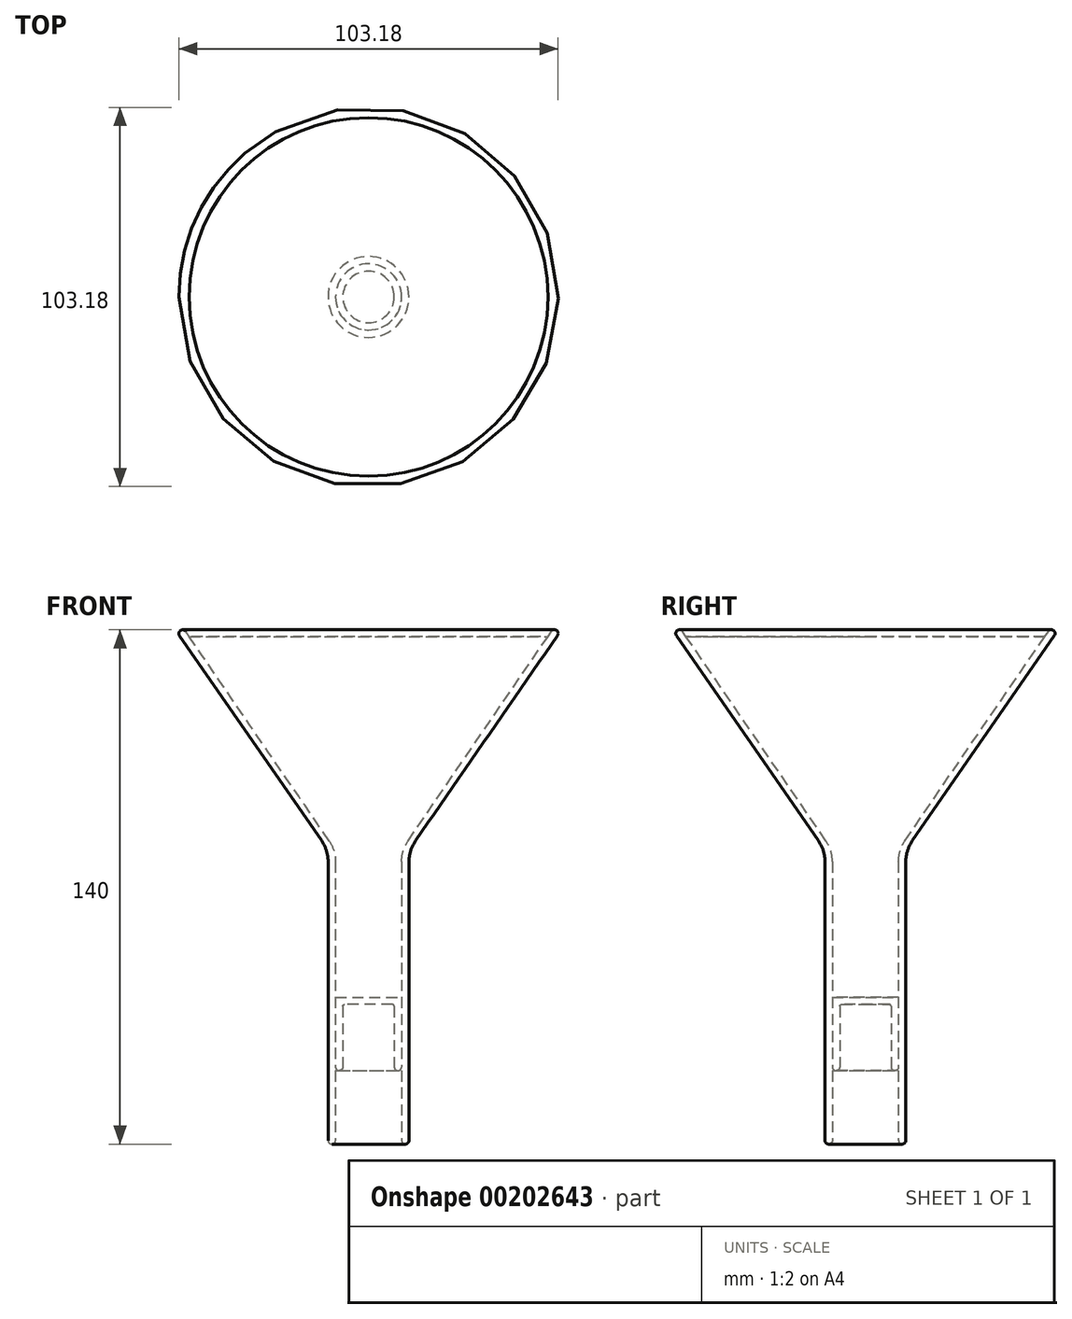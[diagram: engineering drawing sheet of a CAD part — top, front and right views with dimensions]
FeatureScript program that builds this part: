
annotation { "Feature Type Name" : "Feature", "Feature Type Description" : "" }
export const myFeature = defineFeature(function(context is Context, id is Id, definition is map)
    precondition{}
    {
        {
            var Q0;
            Q0=qCreatedBy(makeId("Front.planeOp"),FACE);
            var sketch = newSketch(context, id + "F0", { "sketchPlane" : qUnion([Q0])});
            skLineSegment(sketch, "E0", {"start": v(0, 91.4) * mm, "end": v(0, -48.6) * mm});
            skLineSegment(sketch, "E1", {"start": v(-50.07, 91.4) * mm, "end": v(-52.5, 91.4) * mm});
            skLineSegment(sketch, "E2", {"start": v(-11, -48.6) * mm, "end": v(-11, 31.4) * mm});
            skLineSegment(sketch, "E3", {"start": v(-52.5, 91.4) * mm, "end": v(-11, 31.4) * mm});
            skLineSegment(sketch, "E4.0", {"start": v(-9, -48.6) * mm, "end": v(-9, -28.6) * mm});
            skLineSegment(sketch, "E4.1", {"start": v(-50.07, 91.4) * mm, "end": v(-48.8, 89.57) * mm});
            skPoint(sketch, "E5.start.orphan", {"position": v(-5.5, -48.6) * mm});
            skLineSegment(sketch, "E6.trimOffspring", {"start": v(-9, -48.6) * mm, "end": v(-11, -48.6) * mm});
            skSolve(sketch);
        }
        {
            var Q0;
            Q0 = qSketchRegion(id + "F0", true);
            var Q1;
            Q1=sQuery(id+"F0.wireOp",EDGE,"E4.0");
            var Q2;
            Q2=sQuery(id+"F0.wireOp",EDGE,"E2");
            var Q3;
            Q3=sQuery(id+"F0.wireOp",EDGE,"E3");
            var Q4;
            Q4=sQuery(id+"F0.wireOp",EDGE,"E4.1");
            var Q5;
            Q5=sQuery(id+"F0.wireOp",EDGE,"E6.trimOffspring");
            var Q6;
            Q6=sQuery(id+"F0.wireOp",EDGE,"E1");
            var Q7;
            Q7=sQuery(id+"F0.wireOp",EDGE,"E0");
            revolve(context, id + "F1", {"bodyType" : ToolBodyType.SURFACE, "entities" : qUnion([Q0]), "surfaceEntities" : qUnion([Q1, Q2, Q3, Q4, Q5, Q6]), "axis" : qUnion([Q7]), "revolveType" : RevolveType.FULL});
        }
        {
            var Q0;
            Q0=qCreatedBy(makeId("Front.planeOp"),FACE);
            var sketch = newSketch(context, id + "F2", { "sketchPlane" : qUnion([Q0])});
            skLineSegment(sketch, "E7.0", {"start": v(-9, -28.6) * mm, "end": v(9, -28.6) * mm});
            skLineSegment(sketch, "E8.bottom", {"start": v(-9, -28.6) * mm, "end": v(-7, -28.6) * mm});
            skLineSegment(sketch, "E8.top", {"start": v(-9, -8.6) * mm, "end": v(0, -8.6) * mm});
            skLineSegment(sketch, "E8.left", {"start": v(-9, -28.6) * mm, "end": v(-9, -8.6) * mm});
            skLineSegment(sketch, "E9.1", {"start": v(-7, -10.6) * mm, "end": v(0, -10.6) * mm});
            skLineSegment(sketch, "E9.2", {"start": v(-7, -28.6) * mm, "end": v(-7, -10.6) * mm});
            skLineSegment(sketch, "E10", {"start": v(0, -7.2) * mm, "end": v(0, -14.21) * mm});
            skPoint(sketch, "E10.endSnap0", {"position": v(0, -10.6) * mm});
            skPoint(sketch, "E9.0.end.orphan", {"position": v(7, -10.6) * mm});
            skPoint(sketch, "E8.right.end.orphan", {"position": v(9, -8.6) * mm});
            skSolve(sketch);
        }
        {
            var Q0;
            Q0 = qSketchRegion(id + "F2", true);
            var Q1;
            Q1=sQuery(id+"F2.wireOp",EDGE,"E8.bottom");
            var Q2;
            Q2=sQuery(id+"F2.wireOp",EDGE,"E8.left");
            var Q3;
            Q3=sQuery(id+"F2.wireOp",EDGE,"E9.2");
            var Q4;
            Q4=sQuery(id+"F2.wireOp",EDGE,"E9.1");
            var Q5;
            Q5=sQuery(id+"F2.wireOp",EDGE,"E8.top");
            var Q6;
            Q6=sQuery(id+"F2.wireOp",EDGE,"E10");
            revolve(context, id + "F3", {"bodyType" : ToolBodyType.SURFACE, "entities" : qUnion([Q0]), "surfaceEntities" : qUnion([Q1, Q2, Q3, Q4, Q5]), "axis" : qUnion([Q6]), "revolveType" : RevolveType.FULL});
        }
        {
            var Q0;
            Q0=qCreatedBy(makeId("Front.planeOp"),FACE);
            var sketch = newSketch(context, id + "F4", { "sketchPlane" : qUnion([Q0])});
            skLineSegment(sketch, "E11.0", {"start": v(48.8, 89.57) * mm, "end": v(-48.8, 89.57) * mm});
            skLineSegment(sketch, "E12.0", {"start": v(0, -8.6) * mm, "end": v(-9, -8.6) * mm});
            skLineSegment(sketch, "E13.bottom", {"start": v(-9, -8.6) * mm, "end": v(0, -8.6) * mm});
            skLineSegment(sketch, "E13.left", {"start": v(-9, -8.6) * mm, "end": v(-9, 31.4) * mm});
            skLineSegment(sketch, "E14", {"start": v(-48.8, 89.57) * mm, "end": v(-9, 31.4) * mm});
            skPoint(sketch, "E15.trimOffspring.end.orphan", {"position": v(-11, 31.4) * mm});
            skPoint(sketch, "E16.0.start.orphan", {"position": v(11, 31.4) * mm});
            skPoint(sketch, "E13.right.end.orphan", {"position": v(9, 37.02) * mm});
            skLineSegment(sketch, "E17", {"start": v(0, -8.6) * mm, "end": v(0, -13.98) * mm});
            skPoint(sketch, "E17.endSnap0", {"position": v(0, -8.6) * mm});
            skPoint(sketch, "E18.orphan", {"position": v(9, -8.6) * mm});
            skSolve(sketch);
        }
        {
            var Q0;
            Q0 = qSketchRegion(id + "F4", true);
            var Q1;
            Q1=sQuery(id+"F4.wireOp",EDGE,"E14");
            var Q2;
            Q2=sQuery(id+"F4.wireOp",EDGE,"E13.left");
            var Q3;
            Q3=sQuery(id+"F4.wireOp",EDGE,"E13.bottom");
            var Q4;
            Q4=sQuery(id+"F4.wireOp",EDGE,"E17");
            revolve(context, id + "F5", {"bodyType" : ToolBodyType.SURFACE, "entities" : qUnion([Q0]), "surfaceEntities" : qUnion([Q1, Q2, Q3]), "axis" : qUnion([Q4]), "revolveType" : RevolveType.FULL});
        }
        {
            var Q0;
            Q0=qCreatedBy(makeId("Front.planeOp"),FACE);
            var sketch = newSketch(context, id + "F6", { "sketchPlane" : qUnion([Q0])});
            skLineSegment(sketch, "E19.0", {"start": v(0, 89.57) * mm, "end": v(-48.8, 89.57) * mm});
            skLineSegment(sketch, "E20", {"start": v(0, 89.57) * mm, "end": v(0, 79.26) * mm});
            skPoint(sketch, "E21.orphan", {"position": v(48.8, 89.57) * mm});
            skSolve(sketch);
        }
        {
            var Q0;
            Q0 = qSketchRegion(id + "F6", true);
            var Q1;
            Q1=sQuery(id+"F6.wireOp",EDGE,"E19.0");
            var Q2;
            Q2=sQuery(id+"F6.wireOp",EDGE,"E20");
            revolve(context, id + "F7", {"bodyType" : ToolBodyType.SURFACE, "entities" : qUnion([Q0]), "surfaceEntities" : qUnion([Q1]), "axis" : qUnion([Q2]), "revolveType" : RevolveType.FULL});
        }
        {
            var Q0;
            Q0=makeQuery(id+"F1.opRevolve","SWEPT_FACE",FACE,{"disambiguationData":[OSD([sQuery(id+"F0.wireOp",EDGE,"E1")])]});
            var Q1;
            Q1=makeQuery(id+"F1.opRevolve","SWEPT_FACE",FACE,{"disambiguationData":[OSD([sQuery(id+"F0.wireOp",EDGE,"E6.trimOffspring")])]});
            var Q2;
            Q2=makeQuery(id+"F3.opRevolve","SWEPT_FACE",FACE,{"disambiguationData":[OSD([sQuery(id+"F2.wireOp",EDGE,"E8.bottom")])]});
            fillet(context, id + "F8", {"entities" : qUnion([Q0, Q1, Q2]), "radius" : 1 * mm, "tangentPropagation" : true, "allowEdgeOverflow" : false});
        }
        {
            var Q0;
            Q0=makeQuery(id+"F1.opRevolve","SWEPT_EDGE",EDGE,{"disambiguationData":[OSD([sQuery(id+"F0.wireOp",VERTEX,"E3.end")])]});
            var Q1;
            Q1=makeQuery(id+"F5.opRevolve","SWEPT_EDGE",EDGE,{"disambiguationData":[OSD([sQuery(id+"F4.wireOp",VERTEX,"E13.left.end")])]});
            fillet(context, id + "F9", {"entities" : qUnion([Q0, Q1]), "radius" : 10 * mm, "tangentPropagation" : true, "allowEdgeOverflow" : false});
        }
        {
            var Q0;
            Q0=makeQuery(id+"F3.opRevolve","SWEPT_EDGE",EDGE,{"disambiguationData":[OSD([sQuery(id+"F2.wireOp",VERTEX,"E9.1.start")])]});
            fillet(context, id + "F10", {"entities" : qUnion([Q0]), "radius" : 0.5 * mm, "tangentPropagation" : true, "allowEdgeOverflow" : false});
        }
    });
